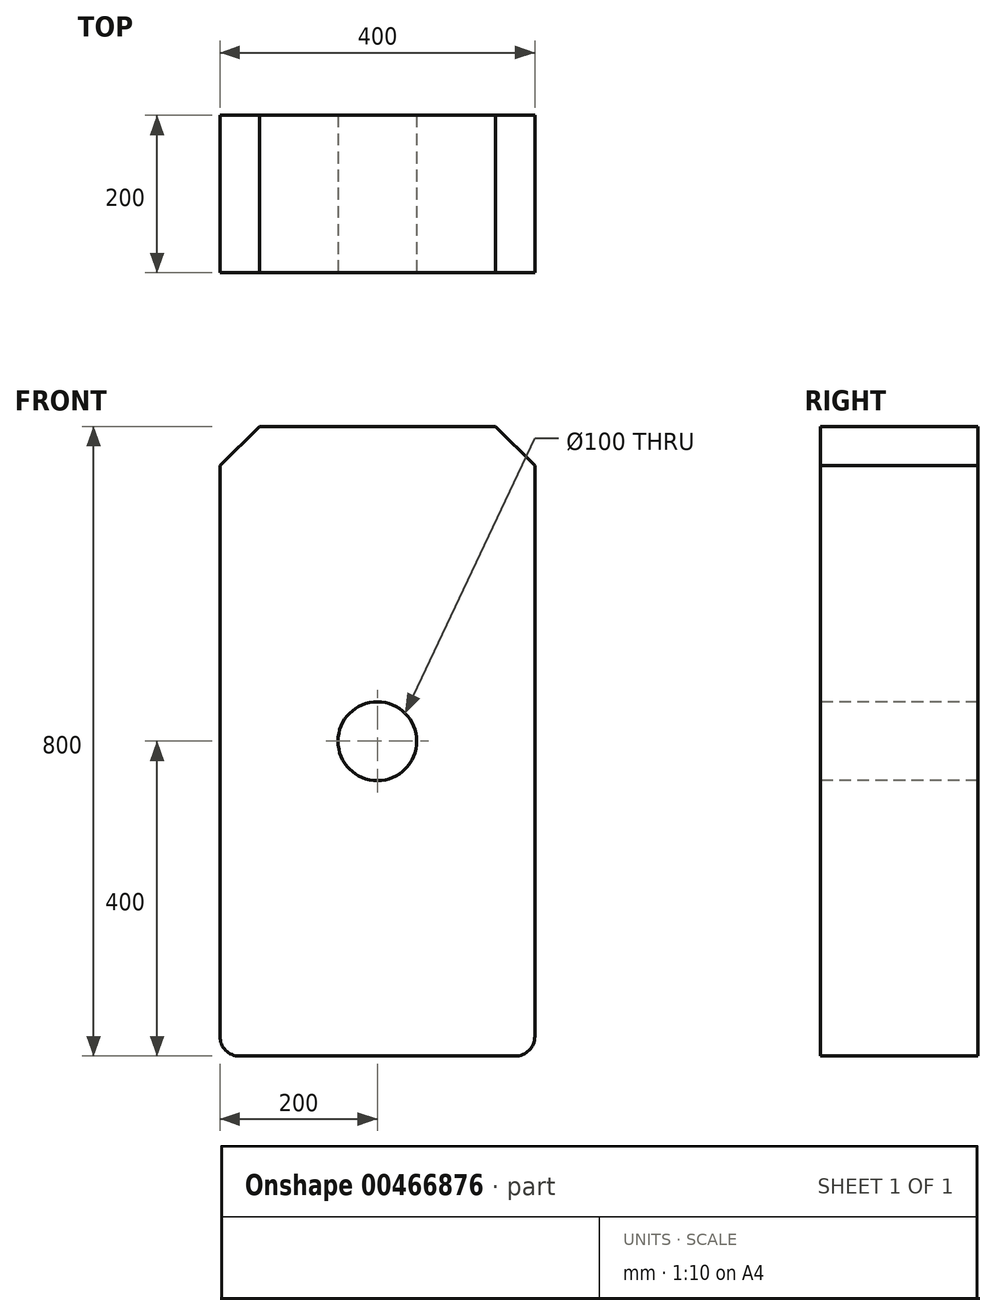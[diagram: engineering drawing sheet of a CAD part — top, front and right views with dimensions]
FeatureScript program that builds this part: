
annotation { "Feature Type Name" : "Feature", "Feature Type Description" : "" }
export const myFeature = defineFeature(function(context is Context, id is Id, definition is map)
    precondition{}
    {
        {
            var Q0;
            Q0=qCreatedBy(makeId("Front.planeOp"),FACE);
            var sketch = newSketch(context, id + "F0", { "sketchPlane" : qUnion([Q0])});
            skLineSegment(sketch, "E0.bottom", {"start": v(-200, -400) * mm, "end": v(200, -400) * mm});
            skLineSegment(sketch, "E0.top", {"start": v(-200, 400) * mm, "end": v(200, 400) * mm});
            skLineSegment(sketch, "E0.left", {"start": v(-200, -400) * mm, "end": v(-200, 400) * mm});
            skLineSegment(sketch, "E0.right", {"start": v(200, -400) * mm, "end": v(200, 400) * mm});
            skPoint(sketch, "E0.middle", {"position": v(0, 0) * mm});
            skSolve(sketch);
        }
        {
            var Q0;
            Q0=makeQuery(id+"F0.imprint","IMPRINT",FACE,{"disambiguationData":[TD([[makeQuery(id+"F0.imprint","IMPRINT",EDGE,{"derivedFrom":sQuery(id+"F0.wireOp",EDGE,"E0.bottom")}),1.0]])]});
            extrude(context, id + "F1", {"entities" : qUnion([Q0]), "depth" : 200 * mm});
        }
        {
            var Q0;
            Q0=makeQuery(id+"F1.opExtrude","SWEPT_EDGE",EDGE,{"disambiguationData":[OSD([sQuery(id+"F0.wireOp",EDGE,"E0.top"),sQuery(id+"F0.wireOp",EDGE,"E0.left")])]});
            var Q1;
            Q1=makeQuery(id+"F1.opExtrude","SWEPT_EDGE",EDGE,{"disambiguationData":[OSD([sQuery(id+"F0.wireOp",EDGE,"E0.top"),sQuery(id+"F0.wireOp",EDGE,"E0.right")])]});
            chamfer(context, id + "F2", {"entities" : qUnion([Q0, Q1]), "width" : 50 * mm, "tangentPropagation" : true});
        }
        {
            var Q0;
            Q0=makeQuery(id+"F1.opExtrude","SWEPT_EDGE",EDGE,{"disambiguationData":[OSD([sQuery(id+"F0.wireOp",EDGE,"E0.bottom"),sQuery(id+"F0.wireOp",EDGE,"E0.left")])]});
            var Q1;
            Q1=makeQuery(id+"F1.opExtrude","SWEPT_EDGE",EDGE,{"disambiguationData":[OSD([sQuery(id+"F0.wireOp",EDGE,"E0.bottom"),sQuery(id+"F0.wireOp",EDGE,"E0.right")])]});
            fillet(context, id + "F3", {"entities" : qUnion([Q0, Q1]), "radius" : 25 * mm, "tangentPropagation" : true, "allowEdgeOverflow" : false});
        }
        {
            var Q0;
            Q0=makeQuery(id+"F1.opExtrude","CAP_FACE",FACE,{"disambiguationData":[OSD([sQuery(id+"F0.wireOp",EDGE,"E0.bottom"),sQuery(id+"F0.wireOp",EDGE,"E0.top"),sQuery(id+"F0.wireOp",EDGE,"E0.left"),sQuery(id+"F0.wireOp",EDGE,"E0.right")])],"isStart":false});
            var sketch = newSketch(context, id + "F4", { "sketchPlane" : qUnion([Q0])});
            skCircle(sketch, "E1", {"center": v(0, 0) * mm, "radius": 50 * mm});
            skSolve(sketch);
        }
        {
            var Q0;
            Q0=makeQuery(id+"F4.imprint","IMPRINT",FACE,{"disambiguationData":[TD([[makeQuery(id+"F4.imprint","IMPRINT",EDGE,{"derivedFrom":sQuery(id+"F4.wireOp",EDGE,"E1")}),1.0]])]});
            extrude(context, id + "F5", {"entities" : qUnion([Q0]), "operationType" : NewBodyOperationType.REMOVE, "endBound" : BoundingType.THROUGH_ALL, "oppositeDirection" : true, "depth" : 25 * mm});
        }
    });
